# Revit family: BuroSeating_Konfurb Eightby4-B
name_source: partatom
category: Furniture
units: mm (PartAtom-declared; Revit-internal decimal feet)

## family parameters
Always vertical = Yes
Cut with Voids When Loaded = No
OmniClass Number = 23.40.70.14.64.11
OmniClass Title = Office Furniture
Room Calculation Point = No
Shared = No
Work Plane-Based = No

## types (2) — shared parameters
Assembly Code = E2020
BaseOffset = 18 mm  [stored 0.0590551 ft]
Description = Trapezoid
FeetDiameter = 50 mm  [stored 0.164042 ft]
FeetInset = 35 mm  [stored 0.114829 ft]
FeetMaterial = BuroSeating_Plastic_Black
Manufacturer = Buro Seating
ModifiedIssue = 20230715.01 $
NominalLength = 1220 mm  [stored 4.00262 ft]
NominalWidth = 610 mm  [stored 2.00131 ft]
ProductGroup = Eightby4
ProductPageURL AU = https://buroseating.com
ProductPageURL NZ = https://buroseating.co.nz
ProductRange = Konfurb
URL = https://buroseating.co.nz
URL AU = https://buroseating.com
WarrantyDescription = Full 5 year guarantee (excluding upholstery)
zero-valued in all types: Default Elevation

## per-type parameters (varying)
| type | Model | NominalHeight |
| 450mm | KON390B | 450 mm  [stored 1.47638 ft] |
| 720mm | KON390H-B | 720 mm  [stored 2.3622 ft] |

note: [stored X ft] marks values corroborated as IEEE doubles in the binary element streams (Revit-internal decimal feet)

## geometry (parser evidence)
native form markers: Sweep x5
no freeform markers — native parametric forms only
